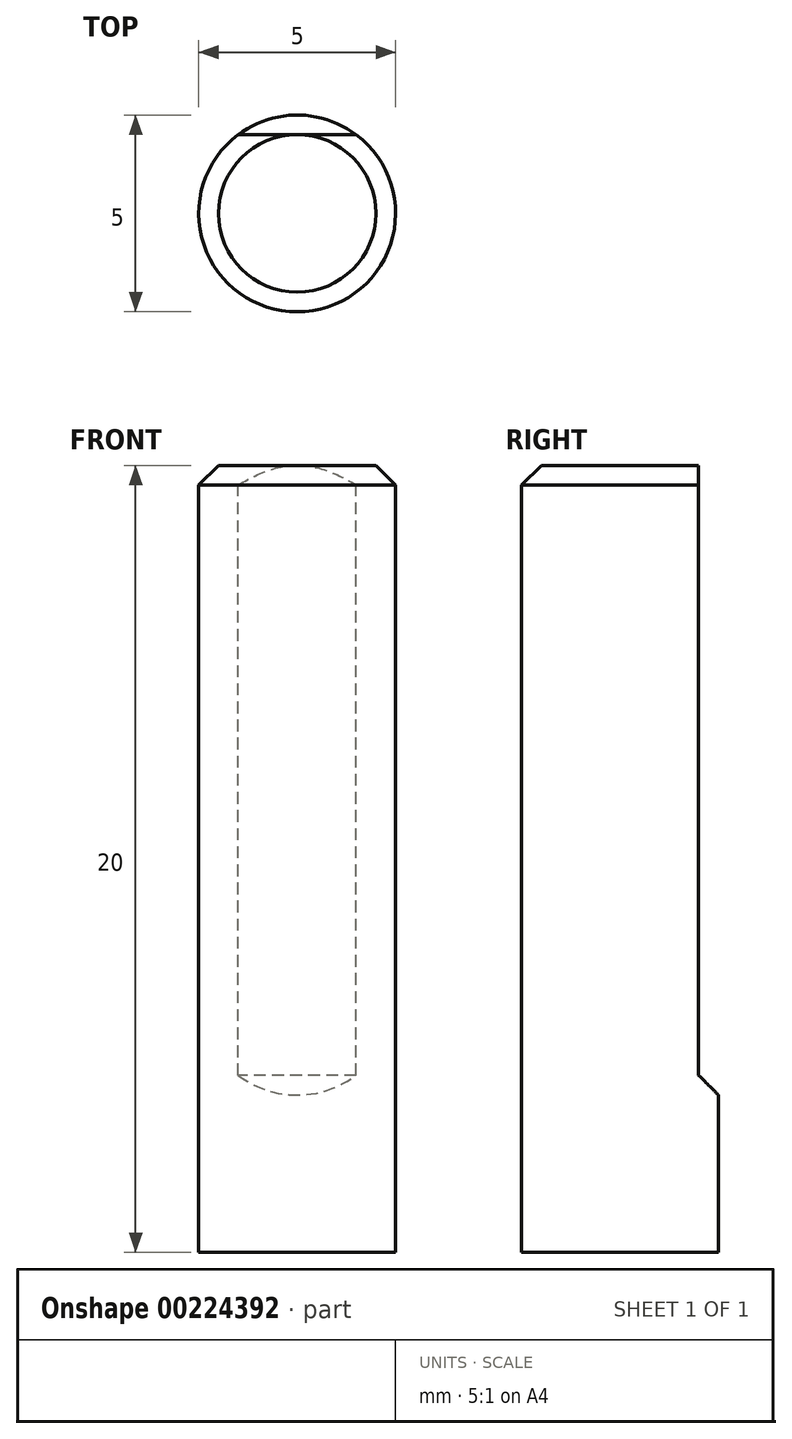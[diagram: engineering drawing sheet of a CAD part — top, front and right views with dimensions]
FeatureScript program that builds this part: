
annotation { "Feature Type Name" : "Feature", "Feature Type Description" : "" }
export const myFeature = defineFeature(function(context is Context, id is Id, definition is map)
    precondition{}
    {
        {
            var Q0;
            Q0=qCreatedBy(makeId("Top.planeOp"),FACE);
            var sketch = newSketch(context, id + "F0", { "sketchPlane" : qUnion([Q0])});
            skCircle(sketch, "E0", {"center": v(0, 0) * mm, "radius": 2.5 * mm});
            skSolve(sketch);
        }
        {
            var Q0;
            Q0=makeQuery(id+"F0.imprint","IMPRINT",FACE,{"disambiguationData":[TD([[makeQuery(id+"F0.imprint","IMPRINT",EDGE,{"derivedFrom":sQuery(id+"F0.wireOp",EDGE,"E0")}),1.0]])]});
            extrude(context, id + "F1", {"entities" : qUnion([Q0]), "depth" : 20 * mm});
        }
        {
            var Q0;
            Q0=makeQuery(id+"F1.opExtrude","CAP_FACE",FACE,{"disambiguationData":[OSD([sQuery(id+"F0.wireOp",EDGE,"E0")])],"isStart":false});
            var sketch = newSketch(context, id + "F2", { "sketchPlane" : qUnion([Q0])});
            skLineSegment(sketch, "E1", {"start": v(-1.5, 2) * mm, "end": v(1.5, 2) * mm});
            skSolve(sketch);
        }
        {
            var Q0;
            {var subQ0=sQuery(id+"F2.wireOp",EDGE,"E1");Q0=makeQuery(id+"F2.imprint","IMPRINT",FACE,{"disambiguationData":[TD([[makeQuery(id+"F2.imprint","IMPRINT",EDGE,{"derivedFrom":subQ0}),1.0]])]});}
            extrude(context, id + "F3", {"entities" : qUnion([Q0]), "operationType" : NewBodyOperationType.REMOVE, "oppositeDirection" : true, "depth" : 16 * mm});
        }
        {
            var Q0;
            Q0=makeQuery(id+"F1.opExtrude","CAP_EDGE",EDGE,{"disambiguationData":[OSD([sQuery(id+"F0.wireOp",EDGE,"E0")])],"isStart":false});
            chamfer(context, id + "F4", {"entities" : qUnion([Q0]), "width" : 0.5 * mm, "tangentPropagation" : true});
        }
        {
            var Q0;
            Q0=makeQuery(id+"F3.boolean.opBoolean","COPY",EDGE,{"derivedFrom":makeQuery(id+"F3.opExtrude","CAP_EDGE",EDGE,{"disambiguationData":[OSD([sQuery(id+"F2.wireOp",EDGE,"E1")])],"isStart":false})});
            chamfer(context, id + "F5", {"entities" : qUnion([Q0]), "width" : 0.5 * mm, "tangentPropagation" : true});
        }
    });
